# Revit family: Carpenters_Window_single
name_source: partatom
category: Windows
units: mm (PartAtom-declared; Revit-internal decimal feet)

## family parameters
Always vertical = Yes
Cut with Voids When Loaded = No
Host = Wall
OmniClass Number = 23.30.20.00
OmniClass Title = Windows
Room Calculation Point = No
Shared = No

## types (3) — shared parameters
Default Sill Height = 800 mm
Define Thermal Properties by = Schematic Type
Glass Thickness = 10 mm  [stored 0.0328084 ft]
Height = 1500 mm
Material Cill - External = <By Category>
Material Cill - Internal = <By Category>
Material Frame = <By Category>
Material Glazing bead = <By Category>
Material Mullions = <By Category>
Material Window = <By Category>
Mullion width = 15 mm  [stored 0.0492126 ft]
Top Panel depth = 600 mm
Wall Closure = By host
Window cill overhang = 25 mm  [stored 0.082021 ft]

## per-type parameters (varying)
| type | Frame depth | Frame width | Material Door | Width | Window setback | Window width |
| 2100x1500mm | 70 mm  [stored 0.229659 ft] | 0 mm  [stored 0 ft] | Door - Panel | 500 mm  [stored 1.64042 ft] | 125 mm  [stored 0.410105 ft] | 50 mm  [stored 0.164042 ft] |
| 2400x1500mm | 100 mm  [stored 0.328084 ft] | 70 mm  [stored 0.229659 ft] | <By Category> | 2400 mm | 75 mm | 75 mm |
| 1800x1500mm | 70 mm  [stored 0.229659 ft] | 20 mm | <By Category> | 1800 mm | 75 mm | 50 mm  [stored 0.164042 ft] |

note: [stored X ft] marks values corroborated as IEEE doubles in the binary element streams (Revit-internal decimal feet)

## geometry (parser evidence)
native form markers: Sweep x3
no freeform markers — native parametric forms only
